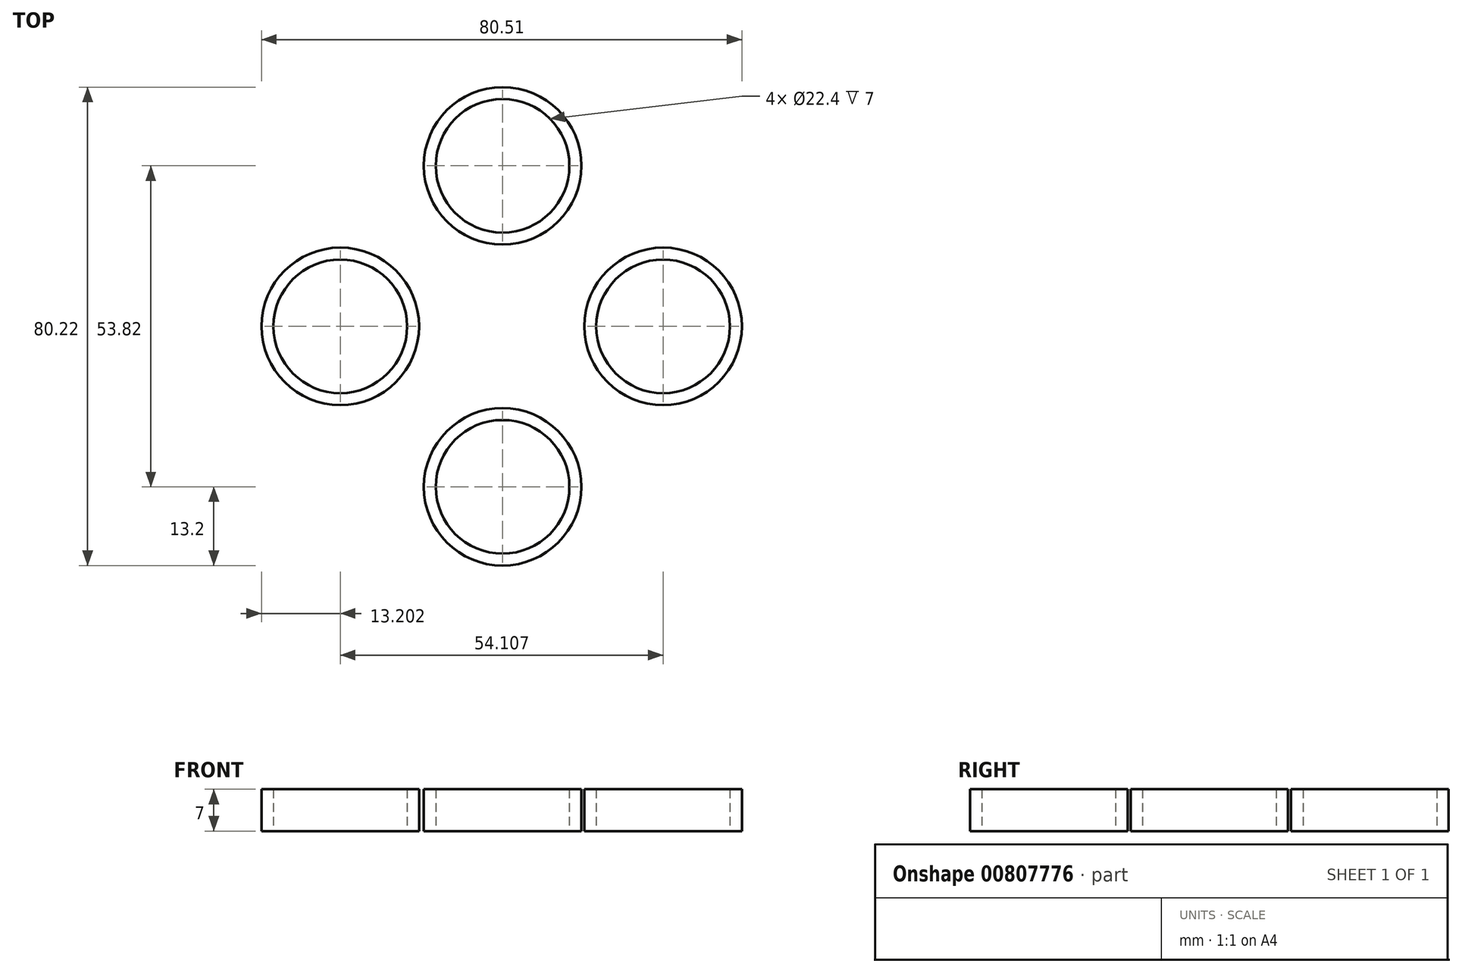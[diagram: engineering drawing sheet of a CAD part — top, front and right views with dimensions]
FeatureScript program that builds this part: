
annotation { "Feature Type Name" : "Feature", "Feature Type Description" : "" }
export const myFeature = defineFeature(function(context is Context, id is Id, definition is map)
    precondition{}
    {
        {
            var Q0;
            Q0=qCreatedBy(makeId("Top.planeOp"),FACE);
            var sketch = newSketch(context, id + "F0", { "sketchPlane" : qUnion([Q0])});
            skCircle(sketch, "E0", {"center": v(0, 0) * mm, "radius": 11.2 * mm});
            skCircle(sketch, "E1", {"center": v(0, 0) * mm, "radius": 11.3 * mm});
            skCircle(sketch, "E2", {"center": v(0, 26.9) * mm, "radius": 11.2 * mm});
            skCircle(sketch, "E3", {"center": v(0, 26.9) * mm, "radius": 13.2 * mm});
            skCircle(sketch, "E4", {"center": v(0, 0) * mm, "radius": 13.2 * mm});
            skCircle(sketch, "E5", {"center": v(0, -26.9) * mm, "radius": 11.2 * mm});
            skCircle(sketch, "E6", {"center": v(0, -26.9) * mm, "radius": 13.2 * mm});
            skCircle(sketch, "E7", {"center": v(26.9, 0) * mm, "radius": 11.2 * mm});
            skCircle(sketch, "E8", {"center": v(26.9, 0) * mm, "radius": 13.2 * mm});
            skCircle(sketch, "E9", {"center": v(-27.2, 0) * mm, "radius": 11.2 * mm});
            skCircle(sketch, "E10", {"center": v(-27.2, 0) * mm, "radius": 13.2 * mm});
            skSolve(sketch);
        }
        {
            var Q0;
            Q0=makeQuery(id+"F0.imprint","IMPRINT",FACE,{"disambiguationData":[TD([[makeQuery(id+"F0.imprint","IMPRINT",EDGE,{"derivedFrom":sQuery(id+"F0.wireOp",EDGE,"E5")}),-1.0]])]});
            var Q1;
            Q1=makeQuery(id+"F0.imprint","IMPRINT",FACE,{"disambiguationData":[TD([[makeQuery(id+"F0.imprint","IMPRINT",EDGE,{"derivedFrom":sQuery(id+"F0.wireOp",EDGE,"E7")}),-1.0]])]});
            var Q2;
            Q2=makeQuery(id+"F0.imprint","IMPRINT",FACE,{"disambiguationData":[TD([[makeQuery(id+"F0.imprint","IMPRINT",EDGE,{"derivedFrom":sQuery(id+"F0.wireOp",EDGE,"E2")}),-1.0]])]});
            var Q3;
            Q3=makeQuery(id+"F0.imprint","IMPRINT",FACE,{"disambiguationData":[TD([[makeQuery(id+"F0.imprint","IMPRINT",EDGE,{"derivedFrom":sQuery(id+"F0.wireOp",EDGE,"E9")}),-1.0]])]});
            extrude(context, id + "F1", {"entities" : qUnion([Q0, Q1, Q2, Q3]), "depth" : 7 * mm, "offsetDistance" : 25 * mm});
        }
    });
